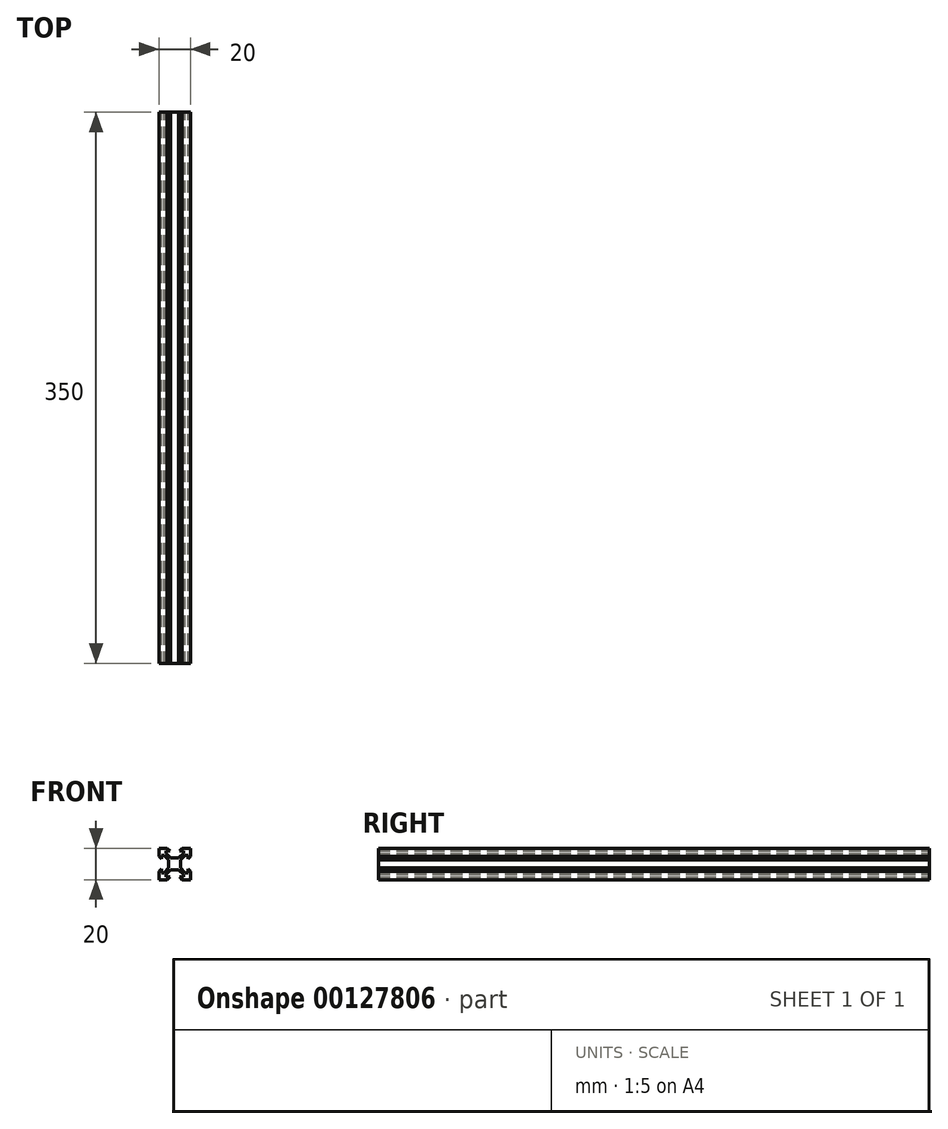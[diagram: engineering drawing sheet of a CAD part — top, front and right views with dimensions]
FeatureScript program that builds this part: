
annotation { "Feature Type Name" : "Feature", "Feature Type Description" : "" }
export const myFeature = defineFeature(function(context is Context, id is Id, definition is map)
    precondition{}
    {
        {
            var Q0;
            Q0=qCreatedBy(makeId("Front.planeOp"),FACE);
            var sketch = newSketch(context, id + "F0", { "sketchPlane" : qUnion([Q0])});
            skLineSegment(sketch, "E0", {"start": v(-10, 10) * mm, "end": v(-4.78, 10) * mm});
            skLineSegment(sketch, "E1", {"start": v(-4.78, 10) * mm, "end": v(-3.1, 8.33) * mm});
            skLineSegment(sketch, "E2", {"start": v(-3.1, 8.32) * mm, "end": v(-5.5, 8.32) * mm});
            skLineSegment(sketch, "E3", {"start": v(-5.5, 8.32) * mm, "end": v(-5.5, 6.68) * mm});
            skLineSegment(sketch, "E4", {"start": v(-5.5, 6.68) * mm, "end": v(-2.57, 3.75) * mm});
            skLineSegment(sketch, "E5", {"start": v(-2.57, 3.75) * mm, "end": v(0, 3.75) * mm});
            skLineSegment(sketch, "E6", {"start": v(0, 0) * mm, "end": v(0, -2.66) * mm, "construction": true});
            skLineSegment(sketch, "E7", {"start": v(0, 0) * mm, "end": v(-3.75, 0) * mm, "construction": true});
            skLineSegment(sketch, "E8", {"start": v(-10, 10) * mm, "end": v(-10, 4.77) * mm});
            skLineSegment(sketch, "E9", {"start": v(-10, 4.78) * mm, "end": v(-8.33, 3.1) * mm});
            skLineSegment(sketch, "E10", {"start": v(-8.32, 3.1) * mm, "end": v(-8.32, 5.5) * mm});
            skLineSegment(sketch, "E11", {"start": v(-8.33, 5.5) * mm, "end": v(-6.68, 5.5) * mm});
            skLineSegment(sketch, "E12", {"start": v(-6.68, 5.5) * mm, "end": v(-3.75, 2.57) * mm});
            skLineSegment(sketch, "E13", {"start": v(-3.75, 2.57) * mm, "end": v(-3.75, 0) * mm});
            skCircle(sketch, "E14", {"center": v(0, 0) * mm, "radius": 2.1 * mm, "construction": true});
            skLineSegment(sketch, "E15.1.0", {"start": v(-5.5, -6.68) * mm, "end": v(-2.57, -3.75) * mm});
            skLineSegment(sketch, "E15.1.1", {"start": v(-5.5, -8.33) * mm, "end": v(-5.5, -6.68) * mm});
            skLineSegment(sketch, "E15.1.2", {"start": v(-3.1, -8.32) * mm, "end": v(-5.5, -8.32) * mm});
            skLineSegment(sketch, "E15.1.3", {"start": v(-4.78, -10) * mm, "end": v(-3.1, -8.33) * mm});
            skLineSegment(sketch, "E15.1.4", {"start": v(-10, -10) * mm, "end": v(-4.77, -10) * mm});
            skLineSegment(sketch, "E15.1.5", {"start": v(-8.32, -5.5) * mm, "end": v(-6.68, -5.5) * mm});
            skLineSegment(sketch, "E15.1.6", {"start": v(-8.32, -3.1) * mm, "end": v(-8.32, -5.5) * mm});
            skLineSegment(sketch, "E15.1.7", {"start": v(-10, -4.77) * mm, "end": v(-8.33, -3.1) * mm});
            skLineSegment(sketch, "E15.1.8", {"start": v(-10, -10) * mm, "end": v(-10, -4.77) * mm});
            skLineSegment(sketch, "E15.1.9", {"start": v(-2.57, -3.75) * mm, "end": v(0, -3.75) * mm});
            skLineSegment(sketch, "E15.1.10", {"start": v(-6.68, -5.5) * mm, "end": v(-3.75, -2.57) * mm});
            skLineSegment(sketch, "E15.1.11", {"start": v(-3.75, -2.57) * mm, "end": v(-3.75, 0) * mm});
            skLineSegment(sketch, "E15.2.0", {"start": v(6.68, -5.5) * mm, "end": v(3.75, -2.57) * mm});
            skLineSegment(sketch, "E15.2.1", {"start": v(8.33, -5.5) * mm, "end": v(6.68, -5.5) * mm});
            skLineSegment(sketch, "E15.2.2", {"start": v(8.32, -3.1) * mm, "end": v(8.32, -5.5) * mm});
            skLineSegment(sketch, "E15.2.3", {"start": v(10, -4.78) * mm, "end": v(8.33, -3.1) * mm});
            skLineSegment(sketch, "E15.2.4", {"start": v(10, -10) * mm, "end": v(10, -4.78) * mm});
            skLineSegment(sketch, "E15.2.5", {"start": v(5.5, -8.32) * mm, "end": v(5.5, -6.68) * mm});
            skLineSegment(sketch, "E15.2.6", {"start": v(3.1, -8.32) * mm, "end": v(5.5, -8.32) * mm});
            skLineSegment(sketch, "E15.2.7", {"start": v(4.77, -10) * mm, "end": v(3.1, -8.33) * mm});
            skLineSegment(sketch, "E15.2.8", {"start": v(10, -10) * mm, "end": v(4.77, -10) * mm});
            skLineSegment(sketch, "E15.2.9", {"start": v(3.75, -2.57) * mm, "end": v(3.75, 0) * mm});
            skLineSegment(sketch, "E15.2.10", {"start": v(5.5, -6.68) * mm, "end": v(2.57, -3.75) * mm});
            skLineSegment(sketch, "E15.2.11", {"start": v(2.57, -3.75) * mm, "end": v(0, -3.75) * mm});
            skLineSegment(sketch, "E15.3.0", {"start": v(5.5, 6.68) * mm, "end": v(2.57, 3.75) * mm});
            skLineSegment(sketch, "E15.3.1", {"start": v(5.5, 8.33) * mm, "end": v(5.5, 6.68) * mm});
            skLineSegment(sketch, "E15.3.2", {"start": v(3.1, 8.32) * mm, "end": v(5.5, 8.32) * mm});
            skLineSegment(sketch, "E15.3.3", {"start": v(4.78, 10) * mm, "end": v(3.1, 8.33) * mm});
            skLineSegment(sketch, "E15.3.4", {"start": v(10, 10) * mm, "end": v(4.78, 10) * mm});
            skLineSegment(sketch, "E15.3.5", {"start": v(8.32, 5.5) * mm, "end": v(6.68, 5.5) * mm});
            skLineSegment(sketch, "E15.3.6", {"start": v(8.32, 3.1) * mm, "end": v(8.32, 5.5) * mm});
            skLineSegment(sketch, "E15.3.7", {"start": v(10, 4.77) * mm, "end": v(8.33, 3.1) * mm});
            skLineSegment(sketch, "E15.3.8", {"start": v(10, 10) * mm, "end": v(10, 4.77) * mm});
            skLineSegment(sketch, "E15.3.9", {"start": v(2.57, 3.75) * mm, "end": v(0, 3.75) * mm});
            skLineSegment(sketch, "E15.3.10", {"start": v(6.68, 5.5) * mm, "end": v(3.75, 2.57) * mm});
            skLineSegment(sketch, "E15.3.11", {"start": v(3.75, 2.57) * mm, "end": v(3.75, 0) * mm});
            skSolve(sketch);
        }
        {
            var Q0;
            Q0=qSketchRegion(id+"F0",true);
            extrude(context, id + "F1", {"entities" : qUnion([Q0]), "endBound" : BoundingType.SYMMETRIC, "depth" : 350 * mm});
        }
    });
